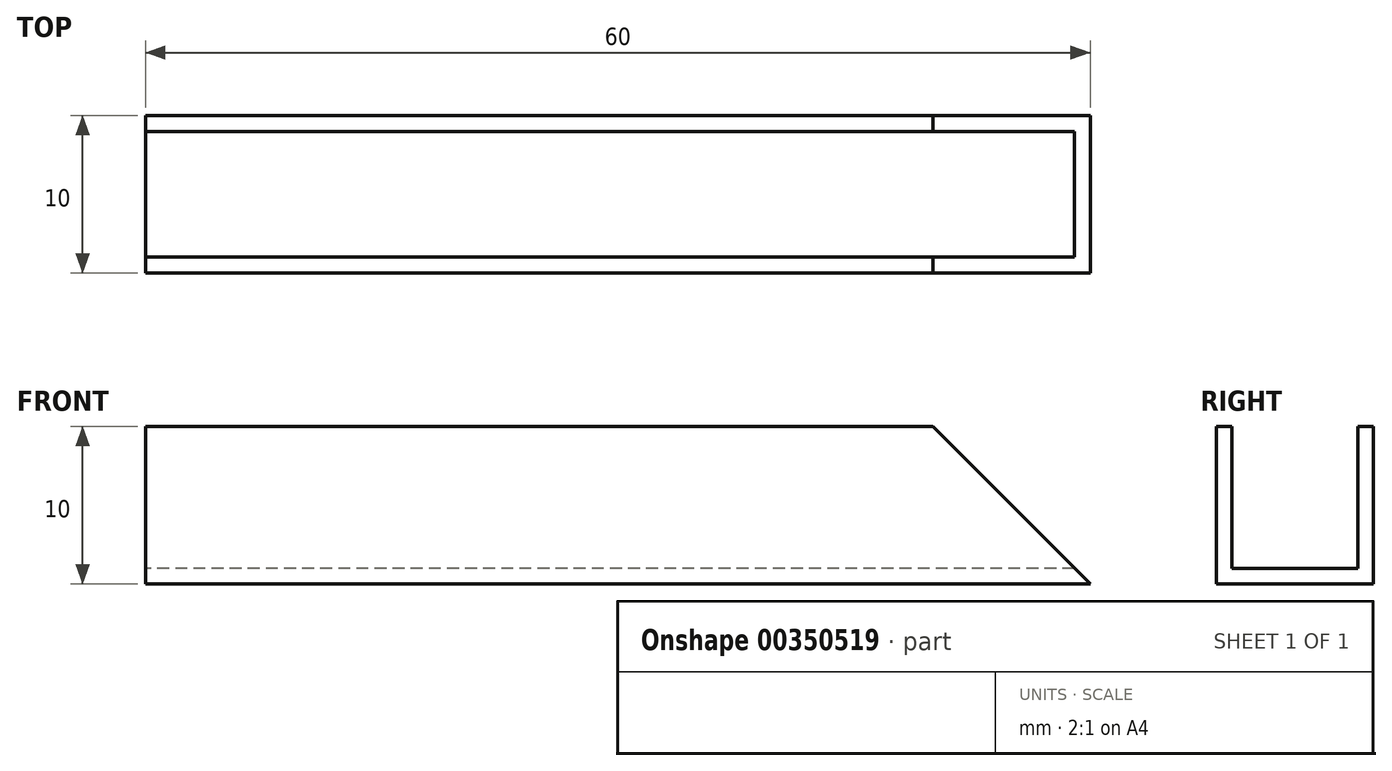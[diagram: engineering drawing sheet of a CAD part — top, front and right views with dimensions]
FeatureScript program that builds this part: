
annotation { "Feature Type Name" : "Feature", "Feature Type Description" : "" }
export const myFeature = defineFeature(function(context is Context, id is Id, definition is map)
    precondition{}
    {
        {
            var Q0;
            Q0=qCreatedBy(makeId("Right.planeOp"),FACE);
            var sketch = newSketch(context, id + "F0", { "sketchPlane" : qUnion([Q0])});
            skLineSegment(sketch, "E0.bottom", {"start": v(-5, 5) * mm, "end": v(5, 5) * mm});
            skLineSegment(sketch, "E0.top", {"start": v(-5, -5) * mm, "end": v(5, -5) * mm});
            skLineSegment(sketch, "E0.left", {"start": v(-5, 5) * mm, "end": v(-5, -5) * mm});
            skLineSegment(sketch, "E0.right", {"start": v(5, 5) * mm, "end": v(5, -5) * mm});
            skPoint(sketch, "E0.middle", {"position": v(0, 0) * mm});
            skLineSegment(sketch, "E1.bottom", {"start": v(-5, 4) * mm, "end": v(5, 4) * mm, "construction": true});
            skLineSegment(sketch, "E1.top", {"start": v(-5, -4) * mm, "end": v(5, -4) * mm, "construction": true});
            skLineSegment(sketch, "E1.left", {"start": v(-5, 4) * mm, "end": v(-5, -4) * mm, "construction": true});
            skLineSegment(sketch, "E1.right", {"start": v(5, 4) * mm, "end": v(5, -4) * mm, "construction": true});
            skLineSegment(sketch, "E2.bottom", {"start": v(-4, 5) * mm, "end": v(4, 5) * mm, "construction": true});
            skLineSegment(sketch, "E2.top", {"start": v(-4, -5) * mm, "end": v(4, -5) * mm, "construction": true});
            skLineSegment(sketch, "E2.left", {"start": v(-4, 5) * mm, "end": v(-4, -5) * mm, "construction": true});
            skLineSegment(sketch, "E2.right", {"start": v(4, 5) * mm, "end": v(4, -5) * mm, "construction": true});
            skLineSegment(sketch, "E3.bottom", {"start": v(-4, 5) * mm, "end": v(4, 5) * mm});
            skLineSegment(sketch, "E3.top", {"start": v(-4, -4) * mm, "end": v(4, -4) * mm});
            skLineSegment(sketch, "E3.left", {"start": v(-4, 5) * mm, "end": v(-4, -4) * mm});
            skLineSegment(sketch, "E3.right", {"start": v(4, 5) * mm, "end": v(4, -4) * mm});
            skSolve(sketch);
        }
        {
            var Q0;
            Q0=makeQuery(id+"F0.imprint","IMPRINT",FACE,{"disambiguationData":[TD([[makeQuery(id+"F0.imprint","IMPRINT",EDGE,{"derivedFrom":sQuery(id+"F0.wireOp",EDGE,"E0.top")}),1.0]])]});
            extrude(context, id + "F1", {"entities" : qUnion([Q0]), "depth" : 60 * mm});
        }
        {
            var Q0;
            {var subQ0=sQuery(id+"F0.wireOp",EDGE,"E0.bottom");Q0=makeQuery(id+"F1.opExtrude","CAP_EDGE",EDGE,{"disambiguationData":[OSD([subQ0]),TDD([makeQuery(id+"F0.imprint","IMPRINT",EDGE,{"disambiguationData":[TD([[makeQuery(id+"F0.imprint","INTERSECT",VERTEX,{"derivedFrom":[subQ0,sQuery(id+"F0.wireOp",EDGE,"E0.left")]}),-1.0]])],"derivedFrom":subQ0})])],"isStart":false});}
            var Q1;
            {var subQ0=sQuery(id+"F0.wireOp",EDGE,"E0.bottom");Q1=makeQuery(id+"F1.opExtrude","CAP_EDGE",EDGE,{"disambiguationData":[OSD([subQ0]),TDD([makeQuery(id+"F0.imprint","IMPRINT",EDGE,{"disambiguationData":[TD([[makeQuery(id+"F0.imprint","INTERSECT",VERTEX,{"derivedFrom":[subQ0,sQuery(id+"F0.wireOp",EDGE,"E0.right")]}),1.0]])],"derivedFrom":subQ0})])],"isStart":false});}
            chamfer(context, id + "F2", {"entities" : qUnion([Q0, Q1]), "width" : 10 * mm, "tangentPropagation" : true});
        }
    });
